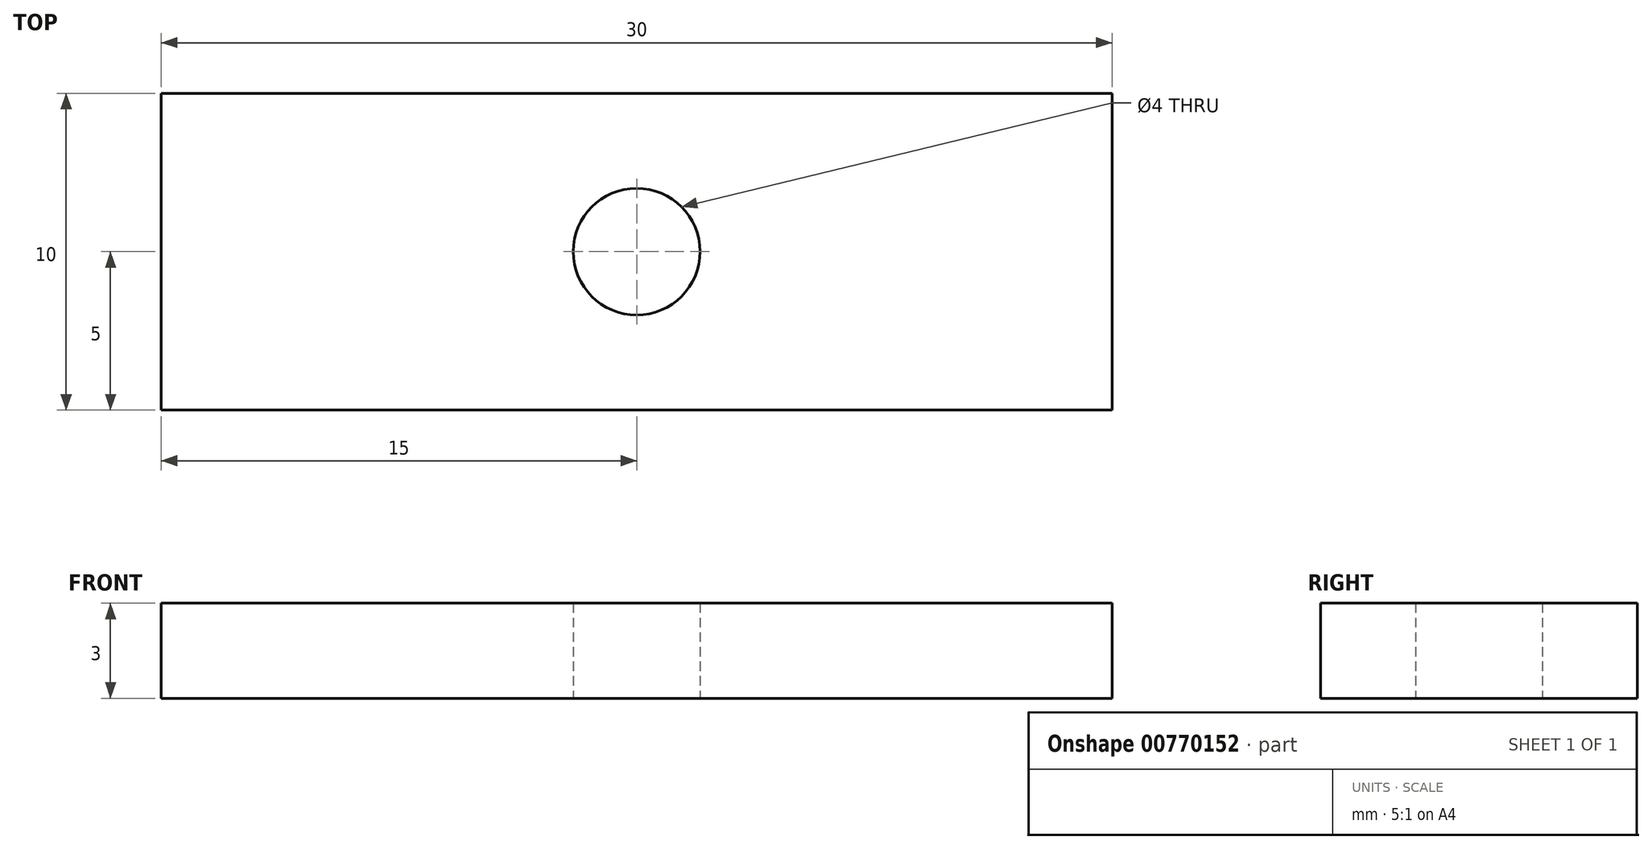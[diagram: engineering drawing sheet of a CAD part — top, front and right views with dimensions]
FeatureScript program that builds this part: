
annotation { "Feature Type Name" : "Feature", "Feature Type Description" : "" }
export const myFeature = defineFeature(function(context is Context, id is Id, definition is map)
    precondition{}
    {
        {
            var Q0;
            Q0=qCreatedBy(makeId("Top.planeOp"),FACE);
            var sketch = newSketch(context, id + "F0", { "sketchPlane" : qUnion([Q0])});
            skLineSegment(sketch, "E0.bottom", {"start": v(-15, 5) * mm, "end": v(15, 5) * mm});
            skLineSegment(sketch, "E0.top", {"start": v(-15, -5) * mm, "end": v(15, -5) * mm});
            skLineSegment(sketch, "E0.left", {"start": v(-15, 5) * mm, "end": v(-15, -5) * mm});
            skLineSegment(sketch, "E0.right", {"start": v(15, 5) * mm, "end": v(15, -5) * mm});
            skPoint(sketch, "E0.middle", {"position": v(0, 0) * mm});
            skCircle(sketch, "E1", {"center": v(0, 0) * mm, "radius": 2 * mm});
            skSolve(sketch);
        }
        {
            var Q0;
            Q0 = qSketchRegion(id + "F0", true);
            extrude(context, id + "F1", {"entities" : qUnion([Q0]), "depth" : 3 * mm, "offsetDistance" : 25 * mm});
        }
    });
